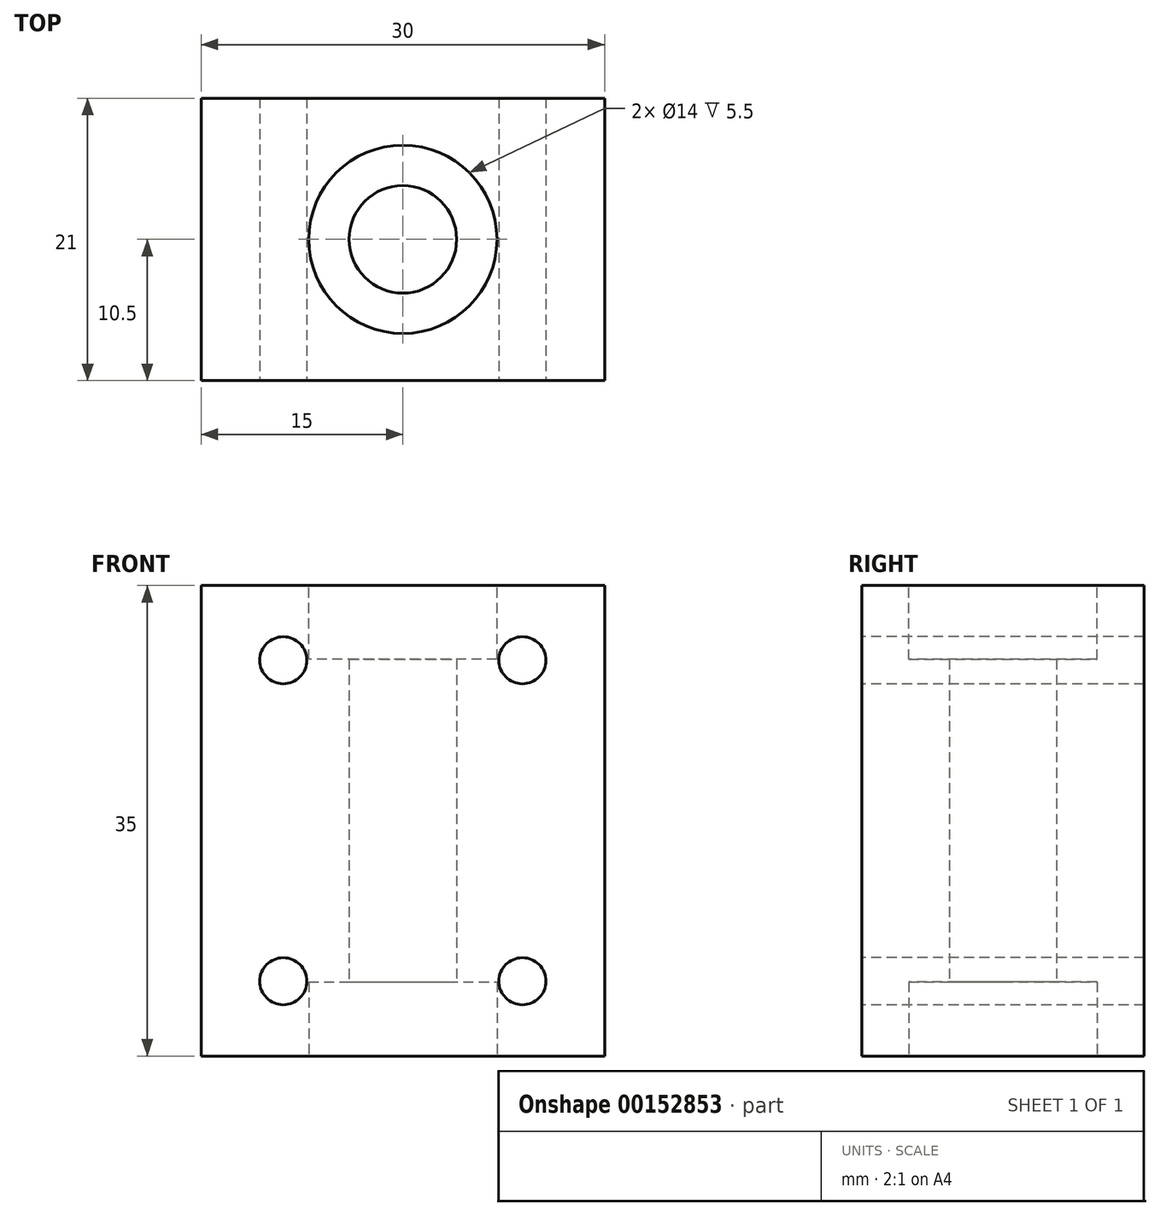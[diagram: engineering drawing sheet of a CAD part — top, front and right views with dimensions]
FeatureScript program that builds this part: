
annotation { "Feature Type Name" : "Feature", "Feature Type Description" : "" }
export const myFeature = defineFeature(function(context is Context, id is Id, definition is map)
    precondition{}
    {
        {
            var Q0;
            Q0=qCreatedBy(makeId("Top.planeOp"),FACE);
            var sketch = newSketch(context, id + "F0", { "sketchPlane" : qUnion([Q0])});
            skCircle(sketch, "E0", {"center": v(0, 0) * mm, "radius": 4 * mm});
            skLineSegment(sketch, "E1.bottom", {"start": v(15, 10.5) * mm, "end": v(-15, 10.5) * mm});
            skLineSegment(sketch, "E1.top", {"start": v(15, -10.5) * mm, "end": v(-15, -10.5) * mm});
            skLineSegment(sketch, "E1.left", {"start": v(15, 10.5) * mm, "end": v(15, -10.5) * mm});
            skLineSegment(sketch, "E1.right", {"start": v(-15, 10.5) * mm, "end": v(-15, -10.5) * mm});
            skSolve(sketch);
        }
        {
            var Q0;
            Q0 = qSketchRegion(id + "F0", true);
            extrude(context, id + "F1", {"entities" : qUnion([Q0]), "depth" : 35 * mm});
        }
        {
            var Q0;
            Q0=makeQuery(id+"F1.opExtrude","CAP_FACE",FACE,{"disambiguationData":[OSD([sQuery(id+"F0.wireOp",EDGE,"E0"),sQuery(id+"F0.wireOp",EDGE,"E1.bottom"),sQuery(id+"F0.wireOp",EDGE,"E1.top"),sQuery(id+"F0.wireOp",EDGE,"E1.left"),sQuery(id+"F0.wireOp",EDGE,"E1.right")])],"isStart":false});
            var sketch = newSketch(context, id + "F2", { "sketchPlane" : qUnion([Q0])});
            skCircle(sketch, "E2", {"center": v(0, 0) * mm, "radius": 7 * mm});
            skSolve(sketch);
        }
        {
            var Q0;
            Q0 = qSketchRegion(id + "F2", true);
            extrude(context, id + "F3", {"entities" : qUnion([Q0]), "operationType" : NewBodyOperationType.REMOVE, "oppositeDirection" : true, "depth" : 5.5 * mm});
        }
        {
            var Q0;
            Q0=makeQuery(id+"F1.opExtrude","CAP_FACE",FACE,{"disambiguationData":[OSD([sQuery(id+"F0.wireOp",EDGE,"E0"),sQuery(id+"F0.wireOp",EDGE,"E1.bottom"),sQuery(id+"F0.wireOp",EDGE,"E1.top"),sQuery(id+"F0.wireOp",EDGE,"E1.left"),sQuery(id+"F0.wireOp",EDGE,"E1.right")])],"isStart":true});
            var sketch = newSketch(context, id + "F4", { "sketchPlane" : qUnion([Q0])});
            skCircle(sketch, "E3", {"center": v(0, 0) * mm, "radius": 7 * mm});
            skSolve(sketch);
        }
        {
            var Q0;
            Q0 = qSketchRegion(id + "F4", true);
            extrude(context, id + "F5", {"entities" : qUnion([Q0]), "operationType" : NewBodyOperationType.REMOVE, "oppositeDirection" : true, "depth" : 5.5 * mm});
        }
        {
            var Q0;
            Q0=makeQuery(id+"F1.opExtrude","SWEPT_FACE",FACE,{"disambiguationData":[OSD([sQuery(id+"F0.wireOp",EDGE,"E1.top")])]});
            var sketch = newSketch(context, id + "F6", { "sketchPlane" : qUnion([Q0])});
            skLineSegment(sketch, "E4", {"start": v(0, 0) * mm, "end": v(0, 35) * mm, "construction": true});
            skLineSegment(sketch, "E5.bottom", {"start": v(-8.89, 5.56) * mm, "end": v(8.9, 5.56) * mm, "construction": true});
            skLineSegment(sketch, "E5.top", {"start": v(-8.9, 29.44) * mm, "end": v(8.89, 29.44) * mm, "construction": true});
            skLineSegment(sketch, "E5.left", {"start": v(-8.9, 5.56) * mm, "end": v(-8.9, 29.44) * mm, "construction": true});
            skLineSegment(sketch, "E5.right", {"start": v(8.9, 5.56) * mm, "end": v(8.9, 29.44) * mm, "construction": true});
            skPoint(sketch, "E5.middle", {"position": v(0, 17.5) * mm});
            skCircle(sketch, "E6", {"center": v(8.9, 5.56) * mm, "radius": 1.75 * mm});
            skCircle(sketch, "E7", {"center": v(-8.89, 5.56) * mm, "radius": 1.75 * mm});
            skCircle(sketch, "E8", {"center": v(8.89, 29.44) * mm, "radius": 1.75 * mm});
            skCircle(sketch, "E9", {"center": v(-8.9, 29.44) * mm, "radius": 1.75 * mm});
            skSolve(sketch);
        }
        {
            var Q0;
            Q0 = qSketchRegion(id + "F6", true);
            var Q1;
            Q1=makeQuery(id+"F1.opExtrude","SWEPT_FACE",FACE,{"disambiguationData":[OSD([sQuery(id+"F0.wireOp",EDGE,"E1.bottom")])]});
            extrude(context, id + "F7", {"entities" : qUnion([Q0]), "operationType" : NewBodyOperationType.REMOVE, "endBound" : BoundingType.UP_TO_SURFACE, "oppositeDirection" : true, "endBoundEntityFace" : qUnion([Q1]), "depth" : 25.4 * mm});
        }
    });
